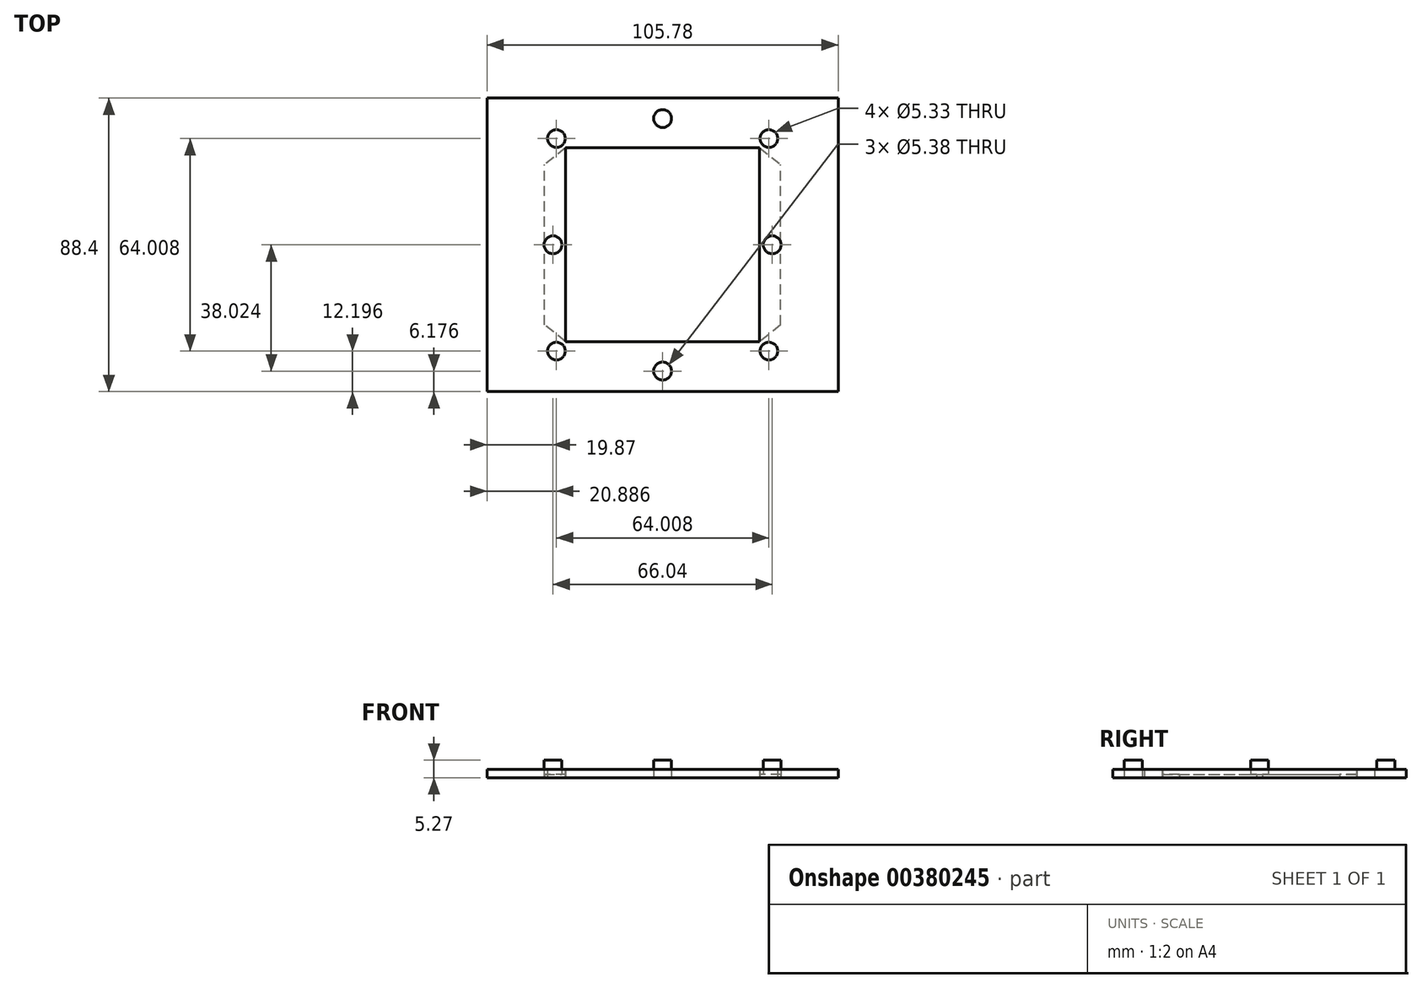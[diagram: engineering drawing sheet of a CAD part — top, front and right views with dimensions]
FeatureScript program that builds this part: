
annotation { "Feature Type Name" : "Feature", "Feature Type Description" : "" }
export const myFeature = defineFeature(function(context is Context, id is Id, definition is map)
    precondition{}
    {
        {
            var Q0;
            Q0=qCreatedBy(makeId("Top.planeOp"),FACE);
            var sketch = newSketch(context, id + "F0", { "sketchPlane" : qUnion([Q0])});
            skLineSegment(sketch, "E0.bottom", {"start": v(29.21, -29.2) * mm, "end": v(-29.21, -29.21) * mm});
            skLineSegment(sketch, "E0.top", {"start": v(29.21, 29.21) * mm, "end": v(-29.2, 29.2) * mm});
            skLineSegment(sketch, "E0.left", {"start": v(29.21, -29.2) * mm, "end": v(29.21, 29.21) * mm});
            skLineSegment(sketch, "E0.right", {"start": v(-29.21, -29.21) * mm, "end": v(-29.2, 29.2) * mm});
            skPoint(sketch, "E0.middle", {"position": v(0, 0) * mm});
            skLineSegment(sketch, "E1.left", {"start": v(35.56, -24.13) * mm, "end": v(35.56, 24.13) * mm});
            skLineSegment(sketch, "E1.right", {"start": v(-35.56, -24.13) * mm, "end": v(-35.56, 24.13) * mm});
            skLineSegment(sketch, "E2", {"start": v(-29.2, 29.2) * mm, "end": v(-35.56, 24.13) * mm});
            skLineSegment(sketch, "E3", {"start": v(29.21, 29.21) * mm, "end": v(35.56, 24.13) * mm});
            skLineSegment(sketch, "E4", {"start": v(35.56, -24.13) * mm, "end": v(29.21, -29.2) * mm});
            skLineSegment(sketch, "E5", {"start": v(-29.21, -29.21) * mm, "end": v(-35.56, -24.13) * mm});
            skLineSegment(sketch, "E6.left", {"start": v(32, -32) * mm, "end": v(32, -29.34) * mm});
            skLineSegment(sketch, "E6.right", {"start": v(-32, -32) * mm, "end": v(-32, -29.34) * mm});
            skCircle(sketch, "E7", {"center": v(-32, 32) * mm, "radius": 2.67 * mm});
            skCircle(sketch, "E8", {"center": v(32, 32) * mm, "radius": 2.67 * mm});
            skCircle(sketch, "E9", {"center": v(32, -32) * mm, "radius": 2.67 * mm});
            skCircle(sketch, "E10", {"center": v(-32, -32) * mm, "radius": 2.67 * mm});
            skLineSegment(sketch, "E11.trimOffspring", {"start": v(-32, 29.34) * mm, "end": v(-32, 32) * mm});
            skLineSegment(sketch, "E12.trimOffspring", {"start": v(32, 29.34) * mm, "end": v(32, 32) * mm});
            skCircle(sketch, "E13", {"center": v(33.02, 0) * mm, "radius": 2.7 * mm});
            skCircle(sketch, "E14.MirrorC", {"center": v(-33.02, 0) * mm, "radius": 2.7 * mm});
            skLineSegment(sketch, "E15", {"start": v(0, 0) * mm, "end": v(0, 38.02) * mm});
            skCircle(sketch, "E16", {"center": v(0, 38.02) * mm, "radius": 2.7 * mm});
            skCircle(sketch, "E17.MirrorC", {"center": v(0, -38.02) * mm, "radius": 2.7 * mm});
            skLineSegment(sketch, "E18.bottom", {"start": v(52.89, 44.2) * mm, "end": v(-52.89, 44.2) * mm});
            skLineSegment(sketch, "E18.top", {"start": v(52.89, -44.2) * mm, "end": v(-52.89, -44.2) * mm});
            skLineSegment(sketch, "E18.left", {"start": v(52.89, 44.2) * mm, "end": v(52.89, -44.2) * mm});
            skLineSegment(sketch, "E18.right", {"start": v(-52.89, 44.2) * mm, "end": v(-52.89, -44.2) * mm});
            skSolve(sketch);
        }
        {
            var Q0;
            Q0 = qSketchRegion(id + "F0", true);
            var Q1;
            Q1=makeQuery(id+"F0.imprint","IMPRINT",FACE,{"disambiguationData":[TD([[makeQuery(id+"F0.imprint","IMPRINT",EDGE,{"derivedFrom":sQuery(id+"F0.wireOp",EDGE,"E0.right")}),1.0]])]});
            var Q2;
            Q2=makeQuery(id+"F0.imprint","IMPRINT",FACE,{"disambiguationData":[TD([[makeQuery(id+"F0.imprint","IMPRINT",EDGE,{"derivedFrom":sQuery(id+"F0.wireOp",EDGE,"E0.left")}),-1.0]])]});
            var Q3;
            Q3=makeQuery(id+"F0.imprint","IMPRINT",FACE,{"disambiguationData":[TD([[makeQuery(id+"F0.imprint","IMPRINT",EDGE,{"derivedFrom":sQuery(id+"F0.wireOp",EDGE,"E16")}),1.0]])]});
            var Q4;
            Q4=makeQuery(id+"F0.imprint","IMPRINT",FACE,{"disambiguationData":[TD([[makeQuery(id+"F0.imprint","IMPRINT",EDGE,{"derivedFrom":sQuery(id+"F0.wireOp",EDGE,"E17.MirrorC")}),-1.0]])]});
            var Q5;
            {var subQ0=sQuery(id+"F0.wireOp",EDGE,"E14.MirrorC");var subQ1=sQuery(id+"F0.wireOp",EDGE,"E1.right");var subQ2=makeQuery(id+"F0.imprint","INTERSECT",VERTEX,{"disambiguationData":[OD(0.0)],"derivedFrom":[subQ1,subQ0]});Q5=makeQuery(id+"F0.imprint","IMPRINT",FACE,{"disambiguationData":[TD([[makeQuery(id+"F0.imprint","IMPRINT",EDGE,{"disambiguationData":[TD([[subQ2,-1.0]])],"derivedFrom":subQ1}),-1.0]])]});}
            var Q6;
            {var subQ0=sQuery(id+"F0.wireOp",EDGE,"E13");var subQ1=sQuery(id+"F0.wireOp",EDGE,"E1.left");var subQ2=makeQuery(id+"F0.imprint","INTERSECT",VERTEX,{"disambiguationData":[OD(0.0)],"derivedFrom":[subQ1,subQ0]});Q6=makeQuery(id+"F0.imprint","IMPRINT",FACE,{"disambiguationData":[TD([[makeQuery(id+"F0.imprint","IMPRINT",EDGE,{"disambiguationData":[TD([[subQ2,-1.0]])],"derivedFrom":subQ1}),1.0]])]});}
            var Q7;
            {var subQ0=sQuery(id+"F0.wireOp",EDGE,"E13");var subQ1=sQuery(id+"F0.wireOp",EDGE,"E1.left");var subQ2=makeQuery(id+"F0.imprint","INTERSECT",VERTEX,{"disambiguationData":[OD(0.0)],"derivedFrom":[subQ1,subQ0]});Q7=makeQuery(id+"F0.imprint","IMPRINT",FACE,{"disambiguationData":[TD([[makeQuery(id+"F0.imprint","IMPRINT",EDGE,{"disambiguationData":[TD([[subQ2,-1.0]])],"derivedFrom":subQ1}),-1.0]])]});}
            var Q8;
            {var subQ0=sQuery(id+"F0.wireOp",EDGE,"E14.MirrorC");var subQ1=sQuery(id+"F0.wireOp",EDGE,"E1.right");var subQ2=makeQuery(id+"F0.imprint","INTERSECT",VERTEX,{"disambiguationData":[OD(0.0)],"derivedFrom":[subQ1,subQ0]});Q8=makeQuery(id+"F0.imprint","IMPRINT",FACE,{"disambiguationData":[TD([[makeQuery(id+"F0.imprint","IMPRINT",EDGE,{"disambiguationData":[TD([[subQ2,-1.0]])],"derivedFrom":subQ1}),1.0]])]});}
            extrude(context, id + "F1", {"entities" : qUnion([Q0, Q1, Q2, Q3, Q4, Q5, Q6, Q7, Q8]), "depth" : 2.57 * mm});
        }
        {
            var Q0;
            Q0=makeQuery(id+"F0.imprint","IMPRINT",FACE,{"disambiguationData":[TD([[makeQuery(id+"F0.imprint","IMPRINT",EDGE,{"derivedFrom":sQuery(id+"F0.wireOp",EDGE,"E0.left")}),-1.0]])]});
            var Q1;
            {var subQ0=sQuery(id+"F0.wireOp",EDGE,"E13");var subQ1=sQuery(id+"F0.wireOp",EDGE,"E1.left");var subQ2=makeQuery(id+"F0.imprint","INTERSECT",VERTEX,{"disambiguationData":[OD(0.0)],"derivedFrom":[subQ1,subQ0]});Q1=makeQuery(id+"F0.imprint","IMPRINT",FACE,{"disambiguationData":[TD([[makeQuery(id+"F0.imprint","IMPRINT",EDGE,{"disambiguationData":[TD([[subQ2,-1.0]])],"derivedFrom":subQ1}),1.0]])]});}
            var Q2;
            Q2=makeQuery(id+"F0.imprint","IMPRINT",FACE,{"disambiguationData":[TD([[makeQuery(id+"F0.imprint","IMPRINT",EDGE,{"derivedFrom":sQuery(id+"F0.wireOp",EDGE,"E0.right")}),1.0]])]});
            var Q3;
            {var subQ0=sQuery(id+"F0.wireOp",EDGE,"E14.MirrorC");var subQ1=sQuery(id+"F0.wireOp",EDGE,"E1.right");var subQ2=makeQuery(id+"F0.imprint","INTERSECT",VERTEX,{"disambiguationData":[OD(0.0)],"derivedFrom":[subQ1,subQ0]});Q3=makeQuery(id+"F0.imprint","IMPRINT",FACE,{"disambiguationData":[TD([[makeQuery(id+"F0.imprint","IMPRINT",EDGE,{"disambiguationData":[TD([[subQ2,-1.0]])],"derivedFrom":subQ1}),-1.0]])]});}
            extrude(context, id + "F2", {"entities" : qUnion([Q0, Q1, Q2, Q3]), "operationType" : NewBodyOperationType.REMOVE, "depth" : 1.02 * mm});
        }
        {
            var Q0;
            Q0=makeQuery(id+"F1.opExtrude","CAP_FACE",FACE,{"disambiguationData":[OSD([sQuery(id+"F0.wireOp",EDGE,"E0.bottom"),sQuery(id+"F0.wireOp",EDGE,"E0.top"),sQuery(id+"F0.wireOp",EDGE,"E0.left"),sQuery(id+"F0.wireOp",EDGE,"E0.right"),sQuery(id+"F0.wireOp",EDGE,"E7"),sQuery(id+"F0.wireOp",EDGE,"E8"),sQuery(id+"F0.wireOp",EDGE,"E9"),sQuery(id+"F0.wireOp",EDGE,"E10"),sQuery(id+"F0.wireOp",EDGE,"E18.bottom"),sQuery(id+"F0.wireOp",EDGE,"E18.top"),sQuery(id+"F0.wireOp",EDGE,"E18.left"),sQuery(id+"F0.wireOp",EDGE,"E18.right")])],"isStart":false});
            var sketch = newSketch(context, id + "F3", { "sketchPlane" : qUnion([Q0])});
            skCircle(sketch, "E19", {"center": v(0, 38.02) * mm, "radius": 2.7 * mm});
            skCircle(sketch, "E20", {"center": v(0, -38.02) * mm, "radius": 2.7 * mm});
            skCircle(sketch, "E21", {"center": v(33.02, 0) * mm, "radius": 2.7 * mm});
            skCircle(sketch, "E22", {"center": v(-33.02, 0) * mm, "radius": 2.7 * mm});
            skSolve(sketch);
        }
        {
            var Q0;
            Q0 = qSketchRegion(id + "F3", true);
            extrude(context, id + "F4", {"entities" : qUnion([Q0]), "operationType" : NewBodyOperationType.ADD, "depth" : 2.7 * mm});
        }
    });
